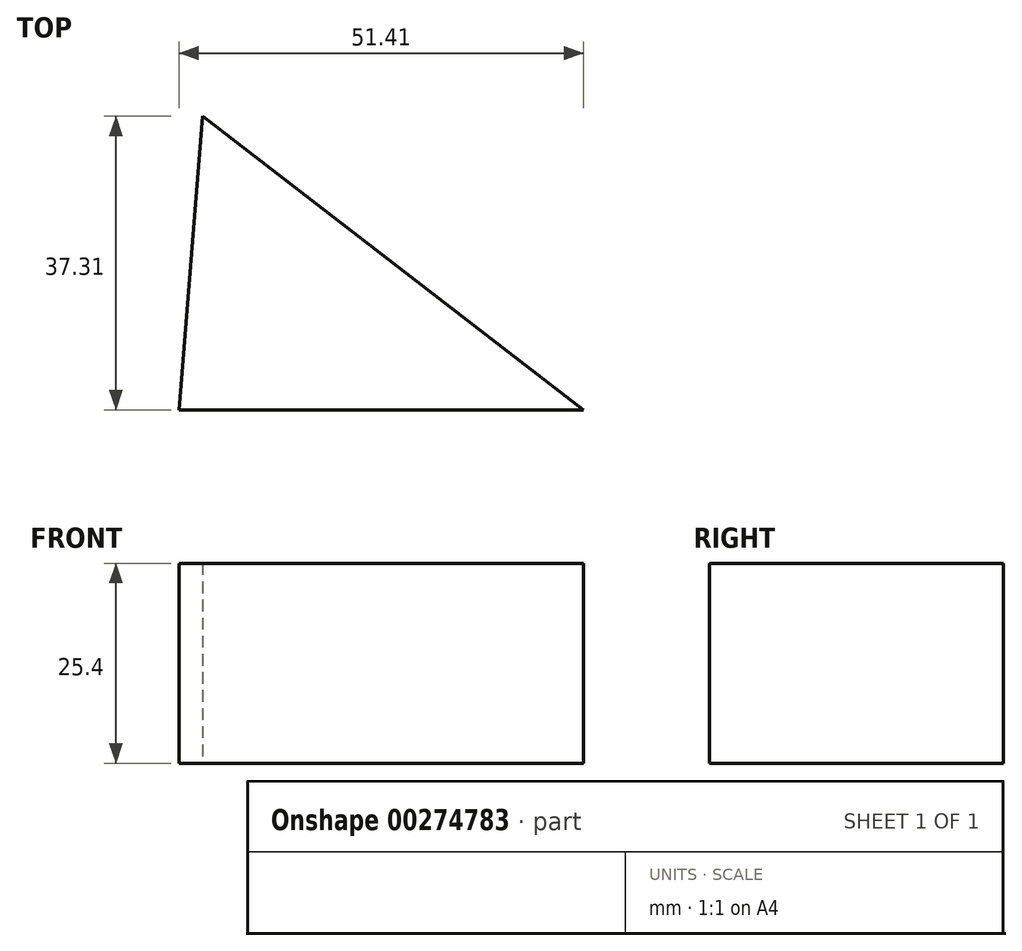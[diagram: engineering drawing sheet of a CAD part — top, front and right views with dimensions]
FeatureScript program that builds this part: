
annotation { "Feature Type Name" : "Feature", "Feature Type Description" : "" }
export const myFeature = defineFeature(function(context is Context, id is Id, definition is map)
    precondition{}
    {
        {
            var Q0;
            Q0=qCreatedBy(makeId("Top.planeOp"),FACE);
            var sketch = newSketch(context, id + "F0", { "sketchPlane" : qUnion([Q0])});
            skLineSegment(sketch, "E0", {"start": v(-107.16, 18.88) * mm, "end": v(-58.77, -18.43) * mm});
            skLineSegment(sketch, "E1", {"start": v(-58.77, -18.43) * mm, "end": v(-110.18, -18.43) * mm});
            skLineSegment(sketch, "E2", {"start": v(-110.18, -18.43) * mm, "end": v(-107.16, 18.88) * mm});
            skSolve(sketch);
        }
        {
            var Q0;
            Q0=makeQuery(id+"F0.imprint","IMPRINT",FACE,{"disambiguationData":[TD([[makeQuery(id+"F0.imprint","IMPRINT",EDGE,{"derivedFrom":sQuery(id+"F0.wireOp",EDGE,"E0")}),-1.0]])]});
            extrude(context, id + "F1", {"entities" : qUnion([Q0]), "depth" : 25.4 * mm});
        }
    });
